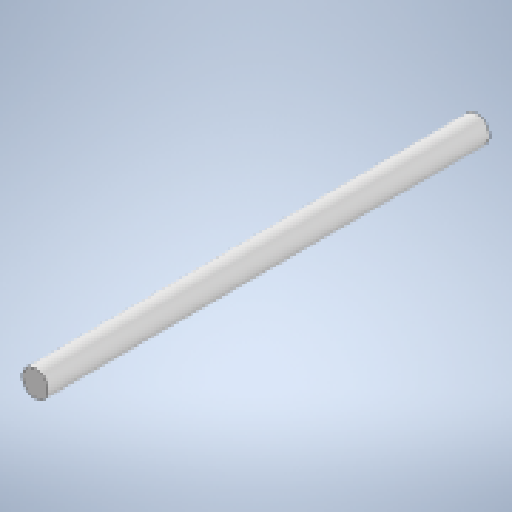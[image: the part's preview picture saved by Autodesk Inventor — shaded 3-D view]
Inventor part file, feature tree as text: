
AUTODESK INVENTOR PART (.ipt)
format: ipt  version: 2023 (Build 270158000, 158)  size: 134,144 bytes
history: native  units: in
note: dims shown in document units (in); Inventor stores cm internally (conversion verified against a paired STEP export)
features: extrude x1, sketch x1
ambient origin geometry x8: Origin, YZ Plane, XZ Plane, XY Plane, X Axis, Y Axis, Z Axis, Center Point
bodies: Solid1 (feature_tree)
feature tree (2):
  extrude  "Extrusion1"  Depth=2.3228in TaperAngle=0.0deg
  sketch  "Sketch1"  dims[d0=0.1378in d1=2.3228in d2=0.0in]
